# Revit family: PRD_FrankeWS_WshbsnTps_ElectronicPillarTap_AQUA135
name_source: partatom
category: Plumbing Fixtures
revit_build: Autodesk Revit 2018 (Build: 20190510_1515(x64)
units: mm (PartAtom-declared; Revit-internal decimal feet)

## family parameters
Always vertical = Yes
Cut with Voids When Loaded = No
OmniClass Number = 23.45.55.14
OmniClass Title = Single Faucets
Part Type = Normal
Room Calculation Point = No
Round Connector Dimension = Use Diameter
Shared = No
Work Plane-Based = Yes

## types (1)
- AQUA135
    ApparentLoad = 0 VA
    AssetType = Fixed
    BIMObjectName = PRD_AR_WashbasinTaps_ElectronicPillarTap_AQUA135
    CalculationFlowRateColdWater = 0.10 liter per second
    Category = Pr_40_20_87_98, Washbasin taps
    Color = Chrome
    Default Elevation = 1219.2 mm  [stored 4 ft]
    DefaultAutomaticHygieneFlushing = Not activated
    DefaultFlowTime = 60.00 seconds
    Depressurised = No
    Description = PROTRONIC-S mains-supplied washbasin tap with touch-free operation, DN 15 with aerator and integrated flow control, for connection to pre-mixed warm or cold water, polished chromium-plated brass. With power supply for installation in the wall, 230 V AC.
    DiameterNominal = 15 mm
    DurationUnit = year
    FaucetFunction = TimedSelfClosing
    FaucetMaterial = PRD_AR_ChromatedBrass_HighPolished
    FaucetOperation = Electronic
    FaucetType = Pillar
    Features = for connection to pre-mixed warm or cold water, polished chromium-plated brass
    Finish = Polished
    FlowColdWater = 0.1 L/s
    FunctionalPrinciple = Electronic self-closing
    GrossWeight = 2.10 kg
    HygieneFlushing = Yes
    IfcExportAs = IfcValveType
    IfcExportType = FAUCET
    InletSize = G3-8
    Manufacturer = KWC Group AG
    ManufacturerName = KWC Group AG
    ManufacturerURL = www.kwc.com
    Material = Brass
    MinimumFlowPressure = 1.00 bar
    Model = AQUA135
    ModelNumber = 2000102697
    ModelReference = AQUA135
    NBSDescription = Water supply fittings for wash basins and troughs
    NBSReference = 45-35-70/371
    Name = Electronic pillar tap AQUA135
    NetWeight = 2.00 kg
    NominalDepth = 0 mm  [stored 0 ft]
    NominalHeight = 179 mm
    NominalWidth = 0 mm  [stored 0 ft]
    PositionOfPowerConnection = From bottom
    PowerFactor = 1
    PowerSupplyConnection = 230 V AC
    ProductInformation = https://pim.kwc.com
    ProtectiveShutdown = Yes
    ProtectiveSystemIP = IP55
    SoundInsulation = 1
    SpoutProjection = 102.00 mm
    ThermalDisinfection = No
    TypeOfFitting = pillar tap
    TypeOfMixing = No mixing
    TypeOfMounting = Tap hole
    TypeOfOperation = Sensor operation
    TypeOfSensor = Opto-electronic sensor
    TypeOfTap = Pillar tap
    URL = www.kwc.com
    Uniclass2015Code = Pr_40_20_87_98
    Uniclass2015Title = Washbasin taps
    Uniclass2015Version = Products v1.17
    Version = 1
    Voltage = 230 V
    VolumeFlowRate = 0.10 l/s at 3 bar
    WarrantyDurationUnit = year

note: [stored X ft] marks values corroborated as IEEE doubles in the binary element streams (Revit-internal decimal feet)

## geometry (parser evidence)
native form markers: Sweep x3
no freeform markers — native parametric forms only
